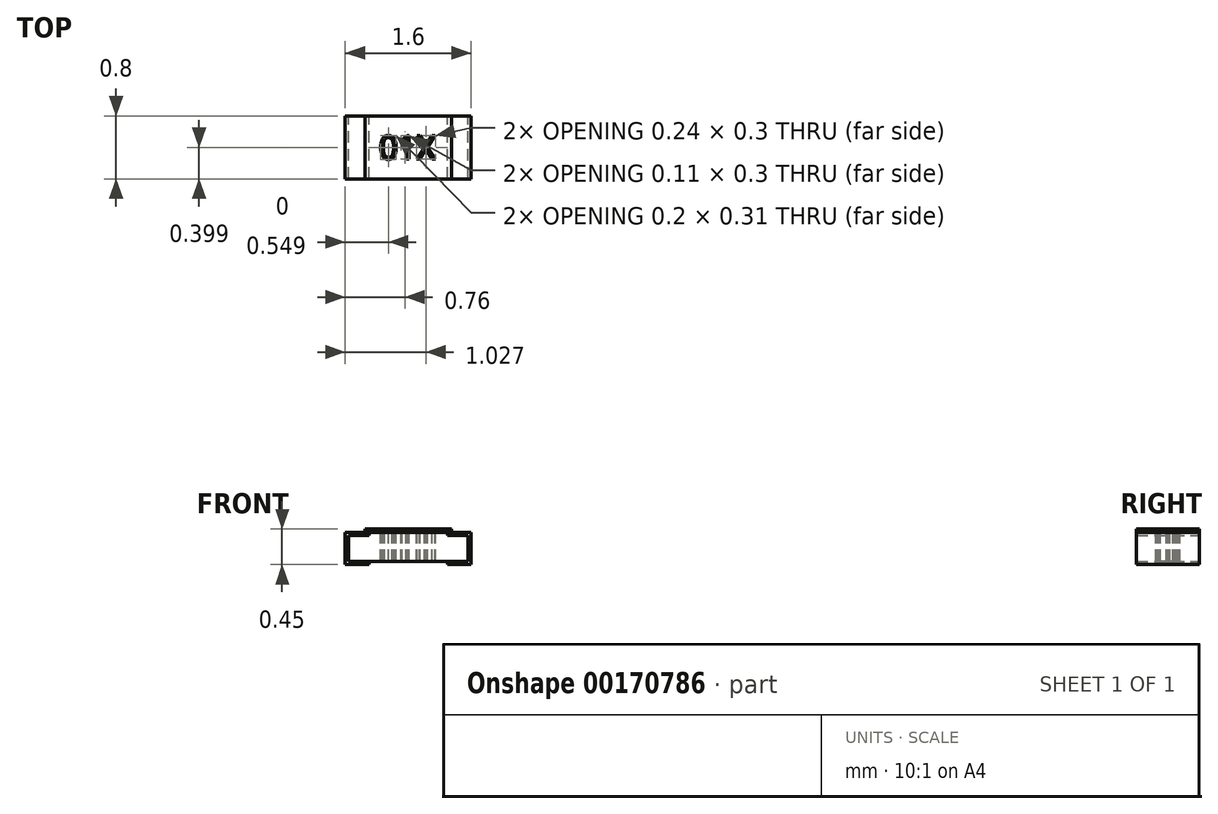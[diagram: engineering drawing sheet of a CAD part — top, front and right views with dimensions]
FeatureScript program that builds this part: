
annotation { "Feature Type Name" : "Feature", "Feature Type Description" : "" }
export const myFeature = defineFeature(function(context is Context, id is Id, definition is map)
    precondition{}
    {
        {
            var Q0;
            Q0=qCreatedBy(makeId("Front.planeOp"),FACE);
            var sketch = newSketch(context, id + "F0", { "sketchPlane" : qUnion([Q0])});
            skLineSegment(sketch, "E0.bottom", {"start": v(-0.76, 0.04) * mm, "end": v(0.76, 0.04) * mm});
            skLineSegment(sketch, "E0.top", {"start": v(-0.76, 0.37) * mm, "end": v(0.76, 0.37) * mm});
            skLineSegment(sketch, "E0.left", {"start": v(-0.76, 0.04) * mm, "end": v(-0.76, 0.37) * mm});
            skLineSegment(sketch, "E0.right", {"start": v(0.76, 0.04) * mm, "end": v(0.76, 0.37) * mm});
            skLineSegment(sketch, "E1", {"start": v(-0.5, 0.37) * mm, "end": v(-0.5, 0.4) * mm});
            skLineSegment(sketch, "E2", {"start": v(-0.5, 0.4) * mm, "end": v(-0.8, 0.4) * mm});
            skLineSegment(sketch, "E3", {"start": v(-0.8, 0.4) * mm, "end": v(-0.8, 0) * mm});
            skLineSegment(sketch, "E4", {"start": v(-0.8, 0) * mm, "end": v(-0.5, 0) * mm});
            skLineSegment(sketch, "E5", {"start": v(-0.5, 0) * mm, "end": v(-0.5, 0.04) * mm});
            skLineSegment(sketch, "E6.MirrorCS", {"start": v(0.5, 0) * mm, "end": v(0.5, 0.04) * mm});
            skLineSegment(sketch, "E7.MirrorCS", {"start": v(0.8, 0) * mm, "end": v(0.5, 0) * mm});
            skLineSegment(sketch, "E8.MirrorCS", {"start": v(0.8, 0.4) * mm, "end": v(0.8, 0) * mm});
            skLineSegment(sketch, "E9.MirrorCS", {"start": v(0.5, 0.37) * mm, "end": v(0.5, 0.4) * mm});
            skLineSegment(sketch, "E10.MirrorCS", {"start": v(0.5, 0.4) * mm, "end": v(0.8, 0.4) * mm});
            skLineSegment(sketch, "E11", {"start": v(-0.55, 0.4) * mm, "end": v(-0.55, 0.45) * mm});
            skLineSegment(sketch, "E12", {"start": v(-0.55, 0.45) * mm, "end": v(0.55, 0.45) * mm});
            skLineSegment(sketch, "E13", {"start": v(0.55, 0.45) * mm, "end": v(0.55, 0.4) * mm});
            skLineSegment(sketch, "E14", {"start": v(-0.5, 0.4) * mm, "end": v(0.5, 0.4) * mm});
            skLineSegment(sketch, "E15", {"start": v(-0.76, 0.37) * mm, "end": v(-0.8, 0.37) * mm, "construction": true});
            skSolve(sketch);
        }
        {
            var Q0;
            {var subQ0=sQuery(id+"F0.wireOp",EDGE,"E0.left");Q0=makeQuery(id+"F0.imprint","IMPRINT",FACE,{"disambiguationData":[TD([[makeQuery(id+"F0.imprint","IMPRINT",EDGE,{"derivedFrom":subQ0}),-1.0]])]});}
            var Q1;
            {var subQ0=sQuery(id+"F0.wireOp",EDGE,"E1");Q1=makeQuery(id+"F0.imprint","IMPRINT",FACE,{"disambiguationData":[TD([[makeQuery(id+"F0.imprint","IMPRINT",EDGE,{"derivedFrom":subQ0}),-1.0]])]});}
            extrude(context, id + "F1", {"entities" : qUnion([Q0, Q1]), "depth" : 0.8 * mm, "offsetDistance" : 25 * mm, "symmetric" : true});
        }
        {
            var Q0;
            {var subQ0=sQuery(id+"F0.wireOp",EDGE,"E0.left");Q0=makeQuery(id+"F0.imprint","IMPRINT",FACE,{"disambiguationData":[TD([[makeQuery(id+"F0.imprint","IMPRINT",EDGE,{"derivedFrom":subQ0}),1.0]])]});}
            var Q1;
            {var subQ1=sQuery(id+"F0.wireOp",EDGE,"E0.right");Q1=makeQuery(id+"F0.imprint","IMPRINT",FACE,{"disambiguationData":[TD([[makeQuery(id+"F0.imprint","IMPRINT",EDGE,{"derivedFrom":subQ1}),-1.0]])]});}
            extrude(context, id + "F2", {"entities" : qUnion([Q0, Q1]), "depth" : 0.8 * mm, "offsetDistance" : 25 * mm, "symmetric" : true});
        }
        {
            var Q0;
            {var subQ0=sQuery(id+"F0.wireOp",EDGE,"E11");Q0=makeQuery(id+"F0.imprint","IMPRINT",FACE,{"disambiguationData":[TD([[makeQuery(id+"F0.imprint","IMPRINT",EDGE,{"derivedFrom":subQ0}),-1.0]])]});}
            extrude(context, id + "F3", {"entities" : qUnion([Q0]), "depth" : 0.8 * mm, "offsetDistance" : 25 * mm, "symmetric" : true});
        }
        {
            var Q0;
            Q0=makeQuery(id+"F3.opExtrude","SWEPT_FACE",FACE,{"disambiguationData":[OSD([sQuery(id+"F0.wireOp",EDGE,"E12")])]});
            var sketch = newSketch(context, id + "F4", { "sketchPlane" : qUnion([Q0])});
            skText(sketch, "E16", { "text": "01X", "fontName": "OpenSans-Regular.ttf"});
            const initialGuessF4  = {"E16": [-0.00037, -0.00015, 1, 0, 0.0003]};
            skSetInitialGuess(sketch, initialGuessF4);
            skSolve(sketch);
        }
        {
            var Q0;
            Q0 = qSketchRegion(id + "F4", true);
            extrude(context, id + "F5", {"entities" : qUnion([Q0]), "operationType" : NewBodyOperationType.REMOVE, "endBound" : BoundingType.THROUGH_ALL, "oppositeDirection" : true, "depth" : 25 * mm, "offsetDistance" : 25 * mm});
        }
    });
